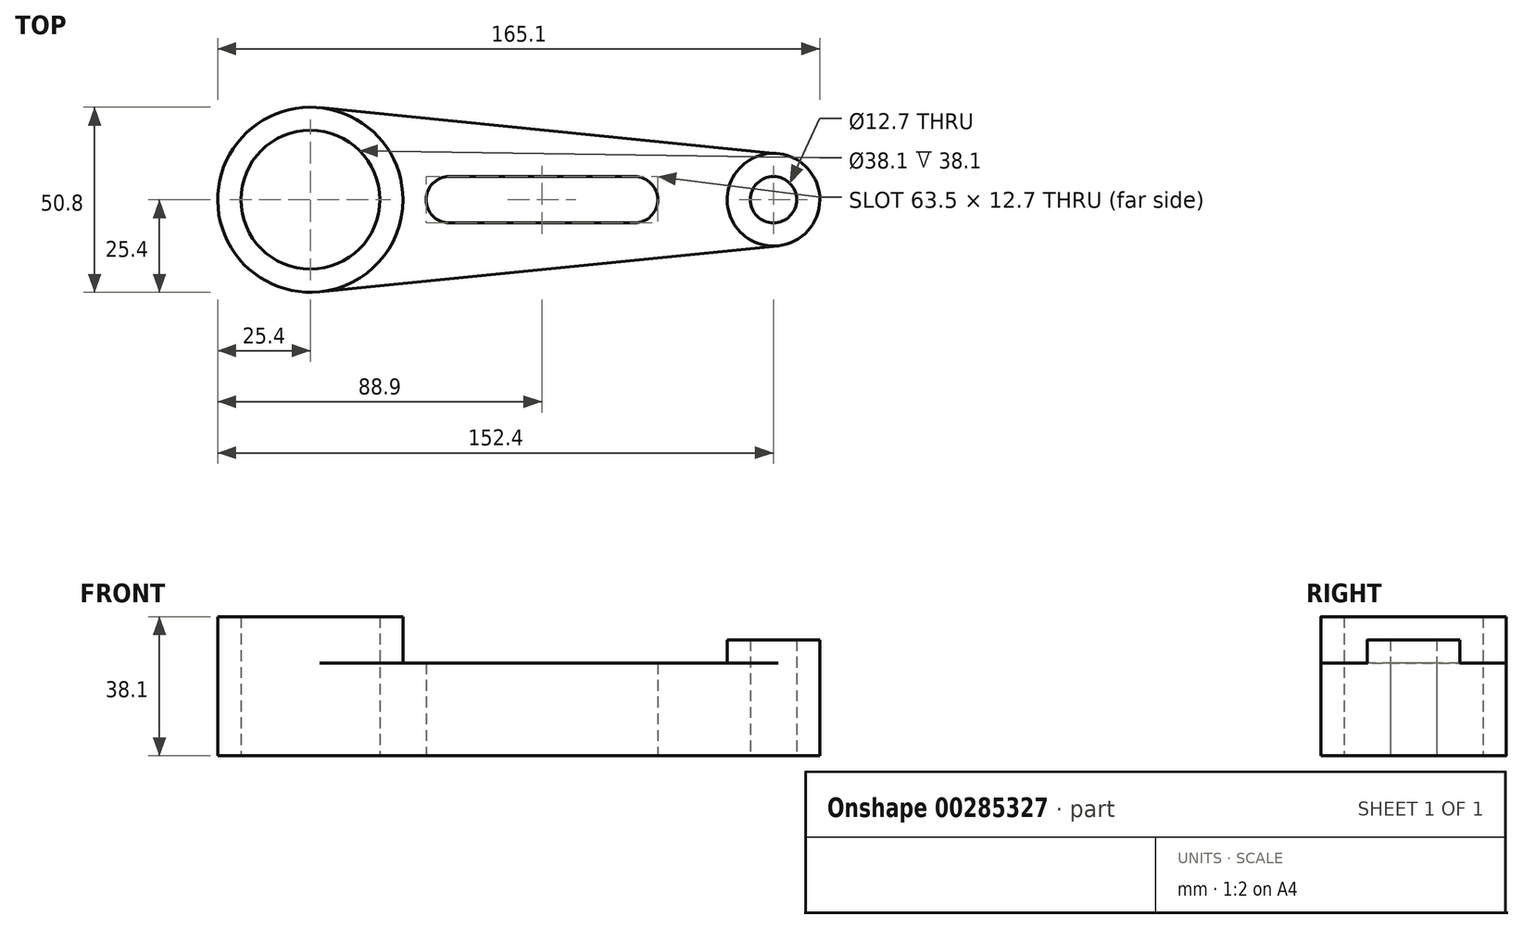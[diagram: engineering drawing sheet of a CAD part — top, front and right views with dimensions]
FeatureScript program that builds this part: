
annotation { "Feature Type Name" : "Feature", "Feature Type Description" : "" }
export const myFeature = defineFeature(function(context is Context, id is Id, definition is map)
    precondition{}
    {
        {
            var Q0;
            Q0=qCreatedBy(makeId("Top.planeOp"),FACE);
            var sketch = newSketch(context, id + "F0", { "sketchPlane" : qUnion([Q0])});
            skCircle(sketch, "E0", {"center": v(0, 0) * mm, "radius": 19.05 * mm});
            skCircle(sketch, "E1", {"center": v(0, 0) * mm, "radius": 25.4 * mm});
            skArc(sketch, "E2", {"start": v(38.1, 6.35) * mm, "mid": v(31.75, 0) * mm, "end": v(38.1, -6.35) * mm});
            skArc(sketch, "E3", {"start": v(88.9, -6.35) * mm, "mid": v(95.25, 0) * mm, "end": v(88.9, 6.35) * mm});
            skCircle(sketch, "E4", {"center": v(127, 0) * mm, "radius": 6.35 * mm});
            skCircle(sketch, "E5", {"center": v(127, 0) * mm, "radius": 12.7 * mm});
            skLineSegment(sketch, "E6", {"start": v(2.54, 25.27) * mm, "end": v(128.27, 12.64) * mm});
            skLineSegment(sketch, "E7", {"start": v(2.54, -25.27) * mm, "end": v(128.27, -12.64) * mm});
            skLineSegment(sketch, "E8", {"start": v(38.1, 6.35) * mm, "end": v(88.9, 6.35) * mm});
            skLineSegment(sketch, "E9", {"start": v(38.1, -6.35) * mm, "end": v(88.9, -6.35) * mm});
            skSolve(sketch);
        }
        {
            var Q0;
            {var subQ3=sQuery(id+"F0.wireOp",EDGE,"E6");Q0=makeQuery(id+"F0.imprint","IMPRINT",FACE,{"disambiguationData":[TD([[makeQuery(id+"F0.imprint","IMPRINT",EDGE,{"derivedFrom":subQ3}),-1.0]])]});}
            extrude(context, id + "F1", {"entities" : qUnion([Q0]), "depth" : 25.4 * mm});
        }
        {
            var Q0;
            Q0=makeQuery(id+"F0.imprint","IMPRINT",FACE,{"disambiguationData":[TD([[makeQuery(id+"F0.imprint","IMPRINT",EDGE,{"derivedFrom":sQuery(id+"F0.wireOp",EDGE,"E4")}),-1.0]])]});
            extrude(context, id + "F2", {"entities" : qUnion([Q0]), "operationType" : NewBodyOperationType.ADD, "depth" : 31.75 * mm});
        }
        {
            var Q0;
            Q0=makeQuery(id+"F0.imprint","IMPRINT",FACE,{"disambiguationData":[TD([[makeQuery(id+"F0.imprint","IMPRINT",EDGE,{"derivedFrom":sQuery(id+"F0.wireOp",EDGE,"E0")}),-1.0]])]});
            extrude(context, id + "F3", {"entities" : qUnion([Q0]), "operationType" : NewBodyOperationType.ADD, "depth" : 38.1 * mm});
        }
    });
